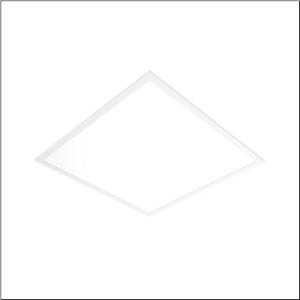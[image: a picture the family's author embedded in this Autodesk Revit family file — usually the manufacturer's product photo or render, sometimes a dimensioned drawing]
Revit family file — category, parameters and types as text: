
# Revit family: apollon_r__41_51mh11wd2443_7c66
name_source: partatom
category: Lighting Fixtures
units: mm (PartAtom-declared; Revit-internal decimal feet)

## family parameters
Cut with Voids When Loaded = No
Host = Face
Light Source = No
Part Type = Normal
Room Calculation Point = No
Round Connector Dimension = Use Diameter
Shared = No

## types (1)
- Apollon® 41 (1 x LED, 3500 lm, 28.5 W, 4000K)
    Apparent Load = 29 VA
    CIE Flux Codes = 61 87 97 100 100
    Color Rendering = 80
    Color Temperature = 4000K
    Default Elevation = 1800 mm
    Description = Apollon® 41, office luminaire, primary optical cover: prismatic diffuser, of PS, light emission: direct distribution, primary light characteristic: symmetric, installation type: lay-in mounting, LED, rated luminous flux: 3.500lm, luminous efficacy: 123lm/W, light colour: 840, colour temperature: 4000K, with terminal, 5-pole, mains connection: 220..240V, AC/DC, 0/50..60Hz, housing, of aluminium section, traffic white (RAL 9016), module: M625, length: 620mm, width: 620mm, height: 28mm, housing upper side, of sheet steel, protection rating (complete): IP20, protection rating (lamp compartment, on room side): IP40, insulation class (complete): insulation class II (safety insulation), certification: CE, ENEC, permissible operating ambient temperature: -25..+40°C, packaging unit: 1 piece
    Height = 0 mm  [stored 0 ft]
    Lamp = 1 x LED
    Lamp Light Flux = 3500 lm
    Lamp Power = 28.5 W
    Lamp count = 1
    Length = 620 mm
    Luminous efficacy = 123 lm/W
    Manufacturer = Siteco
    ModVariant = No
    Model = 51MH11WD2443
    Mounting Place = Ceiling
    Mounting Type = Recessed
    Number of Poles = 1
    OnlyDefault = Yes
    Power Factor = 1
    Product Name = Apollon® 41
    Product group = office luminaire | ceiling recessed
    ProductGroupID = 401
    Protection Class = Protection class II
    Protection Degree = IP 20
    RLX_Detail_Level = 1
    RLX_Emergency_Light_Flux = 0 lm
    RLX_Emergency_Type = 0
    RLX_Emergency_Type_DB = No
    RlxData = <blob elided: 12189 chars, md5=ba4772ad>
    Socket = socket
    Standby Power = 0 W
    System Light Flux = 3500 lm
    System Power = 29 W
    Type Comments = Product without accessories
    Type Image = l_1291024.jpg
    URL = http://relux.com
    VarID = ---
    Voltage = 0 V
    Weight = 0.00 kg
    Width = 620 mm

note: [stored X ft] marks values corroborated as IEEE doubles in the binary element streams (Revit-internal decimal feet)

## geometry (parser evidence)
native form markers: Sweep x11
no freeform markers — native parametric forms only
